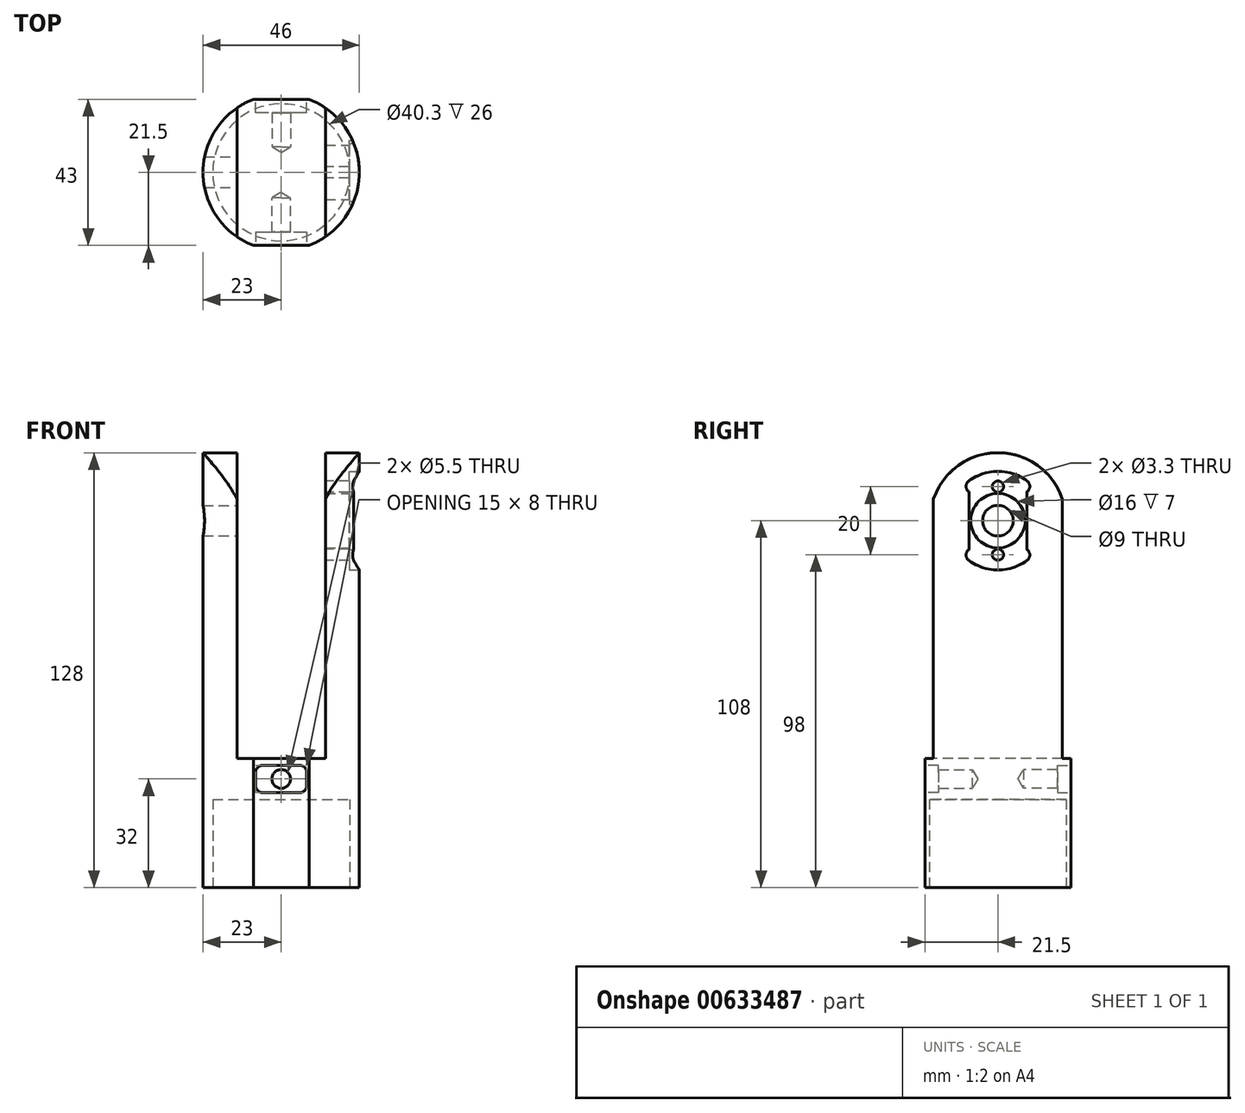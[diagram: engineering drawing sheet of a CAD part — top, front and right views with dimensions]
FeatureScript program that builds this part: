
annotation { "Feature Type Name" : "Feature", "Feature Type Description" : "" }
export const myFeature = defineFeature(function(context is Context, id is Id, definition is map)
    precondition{}
    {
        {
            var Q0;
            Q0=qCreatedBy(makeId("Top.planeOp"),FACE);
            var sketch = newSketch(context, id + "F0", { "sketchPlane" : qUnion([Q0])});
            skArc(sketch, "E0", {"start": v(-8.17, 21.5) * mm, "mid": v(-23, 0) * mm, "end": v(-8.17, -21.5) * mm});
            skLineSegment(sketch, "E1", {"start": v(-8.17, 21.5) * mm, "end": v(8.17, 21.5) * mm});
            skLineSegment(sketch, "E2.MirrorCS", {"start": v(-8.17, -21.5) * mm, "end": v(8.17, -21.5) * mm});
            skArc(sketch, "E3.trimOffspring", {"start": v(8.17, -21.5) * mm, "mid": v(23, 0) * mm, "end": v(8.17, 21.5) * mm});
            skSolve(sketch);
        }
        {
            var Q0;
            Q0 = qSketchRegion(id + "F0", true);
            extrude(context, id + "F1", {"entities" : qUnion([Q0]), "flatOperationType" : FlatOperationType.REMOVE, "depth" : (38 + 90) * mm, "offsetDistance" : 25 * mm, "domain" : OperationDomain.MODEL});
        }
        {
            var Q0;
            Q0=qCreatedBy(makeId("Right.planeOp"),FACE);
            cPlane(context, id + "F2", {"entities" : qUnion([Q0]), "cplaneType" : CPlaneType.OFFSET, "offset" : 23 * mm, "width" : 150 * mm, "height" : 150 * mm});
        }
        {
            var Q0;
            Q0=makeQuery(id+"F1.opExtrude","CAP_FACE",FACE,{"disambiguationData":[OSD([sQuery(id+"F0.wireOp",EDGE,"E0"),sQuery(id+"F0.wireOp",EDGE,"E1"),sQuery(id+"F0.wireOp",EDGE,"E2.MirrorCS"),sQuery(id+"F0.wireOp",EDGE,"E3.trimOffspring")])],"isStart":false});
            var sketch = newSketch(context, id + "F3", { "sketchPlane" : qUnion([Q0])});
            skLineSegment(sketch, "E4.bottom", {"start": v(-13, 23) * mm, "end": v(13, 23) * mm});
            skLineSegment(sketch, "E4.top", {"start": v(-13, -23) * mm, "end": v(13, -23) * mm});
            skLineSegment(sketch, "E4.left", {"start": v(-13, 23) * mm, "end": v(-13, -23) * mm});
            skLineSegment(sketch, "E4.right", {"start": v(13, 23) * mm, "end": v(13, -23) * mm});
            skPoint(sketch, "E4.middle", {"position": v(0, 0) * mm});
            skSolve(sketch);
        }
        {
            var Q0;
            Q0 = qSketchRegion(id + "F3", true);
            extrude(context, id + "F4", {"entities" : qUnion([Q0]), "operationType" : NewBodyOperationType.REMOVE, "flatOperationType" : FlatOperationType.REMOVE, "oppositeDirection" : true, "depth" : 90 * mm, "offsetDistance" : 25 * mm, "domain" : OperationDomain.MODEL});
        }
        {
            var Q0;
            Q0=qCreatedBy(id+"F2.planeOp",FACE);
            var sketch = newSketch(context, id + "F5", { "sketchPlane" : qUnion([Q0])});
            skArc(sketch, "E5", {"start": v(20, 108.55) * mm, "mid": v(-0.02, 128) * mm, "end": v(-20, 108.51) * mm});
            skLineSegment(sketch, "E6", {"start": v(-20, 108.51) * mm, "end": v(-20, 131.37) * mm});
            skLineSegment(sketch, "E7", {"start": v(-20, 131.37) * mm, "end": v(24.18, 131.37) * mm});
            skLineSegment(sketch, "E8", {"start": v(24.18, 131.37) * mm, "end": v(20, 108.55) * mm});
            skSolve(sketch);
        }
        {
            var Q0;
            Q0 = qSketchRegion(id + "F5", true);
            extrude(context, id + "F6", {"entities" : qUnion([Q0]), "operationType" : NewBodyOperationType.REMOVE, "flatOperationType" : FlatOperationType.REMOVE, "endBound" : BoundingType.THROUGH_ALL, "oppositeDirection" : true, "depth" : 25 * mm, "offsetDistance" : 25 * mm, "domain" : OperationDomain.MODEL});
        }
        {
            var Q0;
            Q0=qCreatedBy(id+"F2.planeOp",FACE);
            var sketch = newSketch(context, id + "F7", { "sketchPlane" : qUnion([Q0])});
            skArc(sketch, "E9", {"start": v(-8.55, 96.29) * mm, "mid": v(0, 93.5) * mm, "end": v(8.55, 96.29) * mm});
            skLineSegment(sketch, "E10", {"start": v(0, 127.22) * mm, "end": v(0, 89.88) * mm, "construction": true});
            skLineSegment(sketch, "E11", {"start": v(-8.55, 116.48) * mm, "end": v(-8.55, 99.52) * mm});
            skLineSegment(sketch, "E12.MirrorCS", {"start": v(8.55, 116.48) * mm, "end": v(8.55, 99.52) * mm});
            skArc(sketch, "E13.trimOffspring", {"start": v(8.55, 119.71) * mm, "mid": v(0, 122.5) * mm, "end": v(-8.55, 119.71) * mm});
            skArc(sketch, "E14", {"start": v(-8.55, 119.71) * mm, "mid": v(-9.37, 118.1) * mm, "end": v(-8.55, 116.48) * mm});
            skArc(sketch, "E15", {"start": v(-8.55, 96.29) * mm, "mid": v(-9.37, 97.9) * mm, "end": v(-8.55, 99.52) * mm});
            skArc(sketch, "E16.MirrorCS", {"start": v(8.55, 119.71) * mm, "mid": v(9.37, 118.1) * mm, "end": v(8.55, 116.48) * mm});
            skArc(sketch, "E17.MirrorCS", {"start": v(8.55, 96.29) * mm, "mid": v(9.37, 97.9) * mm, "end": v(8.55, 99.52) * mm});
            skSolve(sketch);
        }
        {
            var Q0;
            Q0 = qSketchRegion(id + "F7", true);
            extrude(context, id + "F8", {"entities" : qUnion([Q0]), "operationType" : NewBodyOperationType.REMOVE, "flatOperationType" : FlatOperationType.REMOVE, "oppositeDirection" : true, "depth" : 3 * mm, "offsetDistance" : 25 * mm, "domain" : OperationDomain.MODEL});
        }
        {
            var Q0;
            Q0=makeQuery(id+"F8.boolean.opBoolean","COPY",FACE,{"derivedFrom":makeQuery(id+"F8.opExtrude","CAP_FACE",FACE,{"disambiguationData":[OSD([sQuery(id+"F7.wireOp",EDGE,"E9"),sQuery(id+"F7.wireOp",EDGE,"E11"),sQuery(id+"F7.wireOp",EDGE,"E12.MirrorCS"),sQuery(id+"F7.wireOp",EDGE,"E13.trimOffspring"),sQuery(id+"F7.wireOp",EDGE,"E14"),sQuery(id+"F7.wireOp",EDGE,"E15"),sQuery(id+"F7.wireOp",EDGE,"E16.MirrorCS"),sQuery(id+"F7.wireOp",EDGE,"E17.MirrorCS")])],"isStart":false})});
            var sketch = newSketch(context, id + "F9", { "sketchPlane" : qUnion([Q0])});
            skPoint(sketch, "E18", {"position": v(0, 98) * mm});
            skPoint(sketch, "E19", {"position": v(0, 118) * mm});
            skSolve(sketch);
        }
        {
            var Q0;
            Q0=sQuery(id+"F9.wireOp",VERTEX,"E19");
            var Q1;
            Q1=sQuery(id+"F9.wireOp",VERTEX,"E18");
            var Q2;
            Q2=makeQuery(id+"F1.opExtrude","SWEPT_BODY",BODY,{"disambiguationData":[OSD([sQuery(id+"F0.wireOp",EDGE,"E0"),sQuery(id+"F0.wireOp",EDGE,"E1"),sQuery(id+"F0.wireOp",EDGE,"E2.MirrorCS"),sQuery(id+"F0.wireOp",EDGE,"E3.trimOffspring")])]});
            hole(context, id + "F10", {"style" : HoleStyle.SIMPLE, "endStyle" : HoleEndStyle.BLIND, "standardTappedOrClearance" : lookupTablePath({ "standard" : "ISO", "fit" : "Normal", "size" : "M3", "type" : "Clearance" }), "standardBlindInLast" : lookupTablePath({ "fit" : "Standard", "standard" : "ISO", "size" : "M3", "type" : "Clearance" }), "holeDiameter" : 3.3 * mm, "majorDiameter" : 5 * mm, "holeDepth" : 20 * mm, "isTappedThrough" : true, "tappedDepth" : 5 * mm, "tapClearance" : 4, "startFromSketch" : true, "locations" : qUnion([Q0, Q1]), "scope" : qUnion([Q2])});
        }
        {
            var Q0;
            Q0=makeQuery(id+"F8.boolean.opBoolean","COPY",FACE,{"derivedFrom":makeQuery(id+"F8.opExtrude","CAP_FACE",FACE,{"disambiguationData":[OSD([sQuery(id+"F7.wireOp",EDGE,"E9"),sQuery(id+"F7.wireOp",EDGE,"E11"),sQuery(id+"F7.wireOp",EDGE,"E12.MirrorCS"),sQuery(id+"F7.wireOp",EDGE,"E13.trimOffspring"),sQuery(id+"F7.wireOp",EDGE,"E14"),sQuery(id+"F7.wireOp",EDGE,"E15"),sQuery(id+"F7.wireOp",EDGE,"E16.MirrorCS"),sQuery(id+"F7.wireOp",EDGE,"E17.MirrorCS")])],"isStart":false})});
            var sketch = newSketch(context, id + "F11", { "sketchPlane" : qUnion([Q0])});
            skCircle(sketch, "E20", {"center": v(0, 108) * mm, "radius": 8 * mm});
            skSolve(sketch);
        }
        {
            var Q0;
            Q0 = qSketchRegion(id + "F11", true);
            extrude(context, id + "F12", {"entities" : qUnion([Q0]), "operationType" : NewBodyOperationType.REMOVE, "flatOperationType" : FlatOperationType.REMOVE, "oppositeDirection" : true, "depth" : 25 * mm, "offsetDistance" : 25 * mm, "domain" : OperationDomain.MODEL});
        }
        {
            var Q0;
            Q0=makeQuery(id+"F4.boolean.opBoolean","COPY",FACE,{"derivedFrom":makeQuery(id+"F4.opExtrude","SWEPT_FACE",FACE,{"disambiguationData":[OSD([sQuery(id+"F3.wireOp",EDGE,"E4.left")])]})});
            var sketch = newSketch(context, id + "F13", { "sketchPlane" : qUnion([Q0])});
            skCircle(sketch, "E21", {"center": v(0, 108) * mm, "radius": 4.5 * mm});
            skSolve(sketch);
        }
        {
            var Q0;
            Q0 = qSketchRegion(id + "F13", true);
            extrude(context, id + "F14", {"entities" : qUnion([Q0]), "operationType" : NewBodyOperationType.REMOVE, "flatOperationType" : FlatOperationType.REMOVE, "endBound" : BoundingType.THROUGH_ALL, "oppositeDirection" : true, "depth" : 25 * mm, "offsetDistance" : 25 * mm, "domain" : OperationDomain.MODEL});
        }
        {
            var Q0;
            Q0=makeQuery(id+"F1.opExtrude","CAP_FACE",FACE,{"disambiguationData":[OSD([sQuery(id+"F0.wireOp",EDGE,"E0"),sQuery(id+"F0.wireOp",EDGE,"E1"),sQuery(id+"F0.wireOp",EDGE,"E2.MirrorCS"),sQuery(id+"F0.wireOp",EDGE,"E3.trimOffspring")])],"isStart":true});
            var sketch = newSketch(context, id + "F15", { "sketchPlane" : qUnion([Q0])});
            skCircle(sketch, "E22", {"center": v(0, 0) * mm, "radius": 20.15 * mm});
            skSolve(sketch);
        }
        {
            var Q0;
            Q0 = qSketchRegion(id + "F15", true);
            extrude(context, id + "F16", {"entities" : qUnion([Q0]), "operationType" : NewBodyOperationType.REMOVE, "flatOperationType" : FlatOperationType.REMOVE, "oppositeDirection" : true, "depth" : 26 * mm, "offsetDistance" : 25 * mm, "domain" : OperationDomain.MODEL});
        }
        {
            var Q0;
            Q0=makeQuery(id+"F1.opExtrude","SWEPT_FACE",FACE,{"disambiguationData":[OSD([sQuery(id+"F0.wireOp",EDGE,"E2.MirrorCS")])]});
            var sketch = newSketch(context, id + "F17", { "sketchPlane" : qUnion([Q0])});
            skLineSegment(sketch, "E23.bottom", {"start": v(-5.5, 36) * mm, "end": v(5.5, 36) * mm});
            skLineSegment(sketch, "E23.top", {"start": v(-5.5, 28) * mm, "end": v(5.5, 28) * mm});
            skLineSegment(sketch, "E23.left", {"start": v(-7.5, 34) * mm, "end": v(-7.5, 30) * mm});
            skLineSegment(sketch, "E23.right", {"start": v(7.5, 34) * mm, "end": v(7.5, 30) * mm});
            skPoint(sketch, "E23.middle", {"position": v(0, 32) * mm});
            skPoint(sketch, "E24.visualSharp", {"position": v(-7.5, 36) * mm});
            skArc(sketch, "E24.filletArc", {"start": v(-5.5, 36) * mm, "mid": v(-6.91, 35.41) * mm, "end": v(-7.5, 34) * mm});
            skPoint(sketch, "E25.visualSharp", {"position": v(-7.5, 28) * mm});
            skArc(sketch, "E25.filletArc", {"start": v(-7.5, 30) * mm, "mid": v(-6.91, 28.59) * mm, "end": v(-5.5, 28) * mm});
            skPoint(sketch, "E26.visualSharp", {"position": v(7.5, 28) * mm});
            skArc(sketch, "E26.filletArc", {"start": v(5.5, 28) * mm, "mid": v(6.91, 28.59) * mm, "end": v(7.5, 30) * mm});
            skPoint(sketch, "E27.visualSharp", {"position": v(7.5, 36) * mm});
            skArc(sketch, "E27.filletArc", {"start": v(7.5, 34) * mm, "mid": v(6.91, 35.41) * mm, "end": v(5.5, 36) * mm});
            skSolve(sketch);
        }
        {
            var Q0;
            Q0 = qSketchRegion(id + "F17", true);
            extrude(context, id + "F18", {"entities" : qUnion([Q0]), "operationType" : NewBodyOperationType.REMOVE, "flatOperationType" : FlatOperationType.REMOVE, "oppositeDirection" : true, "depth" : 4 * mm, "offsetDistance" : 25 * mm, "domain" : OperationDomain.MODEL});
        }
        {
            var Q0;
            Q0=makeQuery(id+"F18.boolean.opBoolean","COPY",FACE,{"derivedFrom":makeQuery(id+"F18.opExtrude","CAP_FACE",FACE,{"disambiguationData":[OSD([sQuery(id+"F17.wireOp",EDGE,"E23.bottom"),sQuery(id+"F17.wireOp",EDGE,"E23.top"),sQuery(id+"F17.wireOp",EDGE,"E23.left"),sQuery(id+"F17.wireOp",EDGE,"E23.right"),sQuery(id+"F17.wireOp",EDGE,"E24.filletArc"),sQuery(id+"F17.wireOp",EDGE,"E25.filletArc"),sQuery(id+"F17.wireOp",EDGE,"E26.filletArc"),sQuery(id+"F17.wireOp",EDGE,"E27.filletArc")])],"isStart":false})});
            var sketch = newSketch(context, id + "F19", { "sketchPlane" : qUnion([Q0])});
            skPoint(sketch, "E28", {"position": v(0, 32) * mm});
            skSolve(sketch);
        }
        {
            var Q0;
            Q0=sQuery(id+"F19.wireOp",VERTEX,"E28");
            var Q1;
            Q1=makeQuery(id+"F1.opExtrude","SWEPT_BODY",BODY,{"disambiguationData":[OSD([sQuery(id+"F0.wireOp",EDGE,"E0"),sQuery(id+"F0.wireOp",EDGE,"E1"),sQuery(id+"F0.wireOp",EDGE,"E2.MirrorCS"),sQuery(id+"F0.wireOp",EDGE,"E3.trimOffspring")])]});
            hole(context, id + "F20", {"style" : HoleStyle.SIMPLE, "endStyle" : HoleEndStyle.BLIND, "standardTappedOrClearance" : lookupTablePath({ "standard" : "ISO", "fit" : "Normal", "size" : "M5", "type" : "Clearance" }), "standardBlindInLast" : lookupTablePath({ "fit" : "Standard", "standard" : "ISO", "size" : "M5", "type" : "Clearance" }), "holeDiameter" : 5.5 * mm, "majorDiameter" : 5 * mm, "holeDepth" : 10 * mm, "isTappedThrough" : true, "tappedDepth" : 5 * mm, "tapClearance" : 4, "startFromSketch" : true, "locations" : qUnion([Q0]), "scope" : qUnion([Q1])});
        }
        {
            var Q0;
            Q0=makeQuery(id+"F1.opExtrude","SWEPT_FACE",FACE,{"disambiguationData":[OSD([sQuery(id+"F0.wireOp",EDGE,"E1")])]});
            var sketch = newSketch(context, id + "F21", { "sketchPlane" : qUnion([Q0])});
            skLineSegment(sketch, "E29.bottom", {"start": v(-5.5, 36) * mm, "end": v(5.5, 36) * mm});
            skLineSegment(sketch, "E29.top", {"start": v(-5.5, 28) * mm, "end": v(5.5, 28) * mm});
            skLineSegment(sketch, "E29.left", {"start": v(-7.5, 34) * mm, "end": v(-7.5, 30) * mm});
            skLineSegment(sketch, "E29.right", {"start": v(7.5, 34) * mm, "end": v(7.5, 30) * mm});
            skPoint(sketch, "E29.middle", {"position": v(0, 32) * mm});
            skPoint(sketch, "E30.visualSharp", {"position": v(-7.5, 36) * mm});
            skArc(sketch, "E30.filletArc", {"start": v(-5.5, 36) * mm, "mid": v(-6.91, 35.41) * mm, "end": v(-7.5, 34) * mm});
            skPoint(sketch, "E31.visualSharp", {"position": v(7.5, 28) * mm});
            skArc(sketch, "E31.filletArc", {"start": v(5.5, 28) * mm, "mid": v(6.91, 28.59) * mm, "end": v(7.5, 30) * mm});
            skPoint(sketch, "E32.visualSharp", {"position": v(-7.5, 28) * mm});
            skArc(sketch, "E32.filletArc", {"start": v(-7.5, 30) * mm, "mid": v(-6.91, 28.59) * mm, "end": v(-5.5, 28) * mm});
            skPoint(sketch, "E33.visualSharp", {"position": v(7.5, 36) * mm});
            skArc(sketch, "E33.filletArc", {"start": v(7.5, 34) * mm, "mid": v(6.91, 35.41) * mm, "end": v(5.5, 36) * mm});
            skSolve(sketch);
        }
        {
            var Q0;
            Q0 = qSketchRegion(id + "F21", true);
            extrude(context, id + "F22", {"entities" : qUnion([Q0]), "operationType" : NewBodyOperationType.REMOVE, "flatOperationType" : FlatOperationType.REMOVE, "oppositeDirection" : true, "depth" : 4 * mm, "offsetDistance" : 25 * mm, "domain" : OperationDomain.MODEL});
        }
        {
            var Q0;
            Q0=makeQuery(id+"F22.boolean.opBoolean","COPY",FACE,{"derivedFrom":makeQuery(id+"F22.opExtrude","CAP_FACE",FACE,{"disambiguationData":[OSD([sQuery(id+"F21.wireOp",EDGE,"E29.bottom"),sQuery(id+"F21.wireOp",EDGE,"E29.top"),sQuery(id+"F21.wireOp",EDGE,"E29.left"),sQuery(id+"F21.wireOp",EDGE,"E29.right"),sQuery(id+"F21.wireOp",EDGE,"E30.filletArc"),sQuery(id+"F21.wireOp",EDGE,"E31.filletArc"),sQuery(id+"F21.wireOp",EDGE,"E32.filletArc"),sQuery(id+"F21.wireOp",EDGE,"E33.filletArc")])],"isStart":false})});
            var sketch = newSketch(context, id + "F23", { "sketchPlane" : qUnion([Q0])});
            skPoint(sketch, "E34", {"position": v(0, 32) * mm});
            skSolve(sketch);
        }
        {
            var Q0;
            Q0=sQuery(id+"F23.wireOp",VERTEX,"E34");
            var Q1;
            Q1=makeQuery(id+"F1.opExtrude","SWEPT_BODY",BODY,{"disambiguationData":[OSD([sQuery(id+"F0.wireOp",EDGE,"E0"),sQuery(id+"F0.wireOp",EDGE,"E1"),sQuery(id+"F0.wireOp",EDGE,"E2.MirrorCS"),sQuery(id+"F0.wireOp",EDGE,"E3.trimOffspring")])]});
            hole(context, id + "F24", {"style" : HoleStyle.SIMPLE, "endStyle" : HoleEndStyle.BLIND, "standardTappedOrClearance" : lookupTablePath({ "standard" : "ISO", "fit" : "Normal", "size" : "M5", "type" : "Clearance" }), "standardBlindInLast" : lookupTablePath({ "fit" : "Standard", "standard" : "ISO", "size" : "M5", "type" : "Clearance" }), "holeDiameter" : 5.5 * mm, "majorDiameter" : 5 * mm, "holeDepth" : 10 * mm, "isTappedThrough" : true, "tappedDepth" : 5 * mm, "tapClearance" : 4, "startFromSketch" : true, "locations" : qUnion([Q0]), "scope" : qUnion([Q1])});
        }
    });
